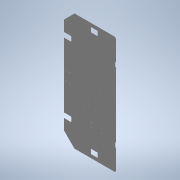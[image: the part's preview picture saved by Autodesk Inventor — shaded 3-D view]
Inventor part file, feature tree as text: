
AUTODESK INVENTOR PART (.ipt)
format: ipt  version: 2022.1 (Build 261234000, 234)  size: 481,792 bytes
history: native  units: mm
features: reference x12, other x11, sketch x3, sheet_metal_op x1, chamfer x1, extrude x1
ambient origin geometry x8: Origin, YZ Plane, XZ Plane, XY Plane, X Axis, Y Axis, Z Axis, Center Point
bodies: Solid1 (feature_tree)
feature tree (29):
  sheet_metal_op  "Face1"
  chamfer  "Corner Round1"
  extrude  "Extrusión1"  Depth=1.0mm
  sketch  "Sketch1"  dims[d1=1.0mm d2=1.0mm]
  reference  "Reference1"
  reference  "Reference2"
  reference  "Reference3"
  reference  "Reference4"
  reference  "Reference5"
  reference  "Reference6"
  other  "Plate1"
  reference  "Reference7"
  reference  "Reference8"
  reference  "Reference9"
  reference  "Reference10"
  reference  "Reference11"
  reference  "Reference12"
  sketch  "Boceto3"  dims[d3=1.0mm]
  sketch  "Boceto4"  dims[d4=1.0mm d5=1.0mm d6=1.0mm d7=1.0mm d10=1.0mm d15=1.0mm d16=0.5mm d17=4.0mm d18=1.0mm d19=1.0mm d20=1.0mm d21=1.0mm d22=1.0mm d24=1.0mm d38=250.0mm d39=67.0mm d40=108.0mm d41=2.9mm d42=2.9mm d43=2.9mm d44=2.9mm d45=250.0mm d46=44.0mm d47=66.0mm d48=1.8mm d49=1.8mm d50=1.8mm d51=1.8mm d52=44.0mm d53=0.0mm d54=66.0mm d55=44.0mm d57=19.0mm d58=44.0mm d59=66.0mm d60=1.8mm d61=1.8mm d62=1.8mm d63=1.8mm d64=1.8mm d65=1.8mm d66=1.8mm d67=1.8mm d68=58.0mm d69=80.0mm d71=4.5mm d72=4.5mm d73=80.0mm d74=95.0mm d75=20.0mm d76=67.0mm d77=108.0mm d78=2.9mm d79=2.9mm d80=2.9mm d81=2.9mm d84=36.9815mm d86=10.0mm d87=92.3mm d88=38.0mm d89=5.0mm d90=3.4mm d91=3.4mm d92=3.4mm d93=3.4mm d101=2.4mm d102=2.4mm d103=30.8356mm d105=20.75mm d106=3.4mm d107=3.4mm d108=3.4mm d109=3.4mm d110=86.999998mm d111=86.999998mm d112=100.269496mm d113=120.0mm d114=80.0mm d115=35.0mm d122=18.159314mm d123=10.372356mm d124=4.5mm d125=4.5mm d126=4.5mm d127=4.5mm d130=80.0mm d131=35.0mm d133=10.372356mm d134=4.5mm d135=4.5mm d136=4.5mm d137=4.5mm d139=12.55mm d140=45.0mm d141=4.5mm d142=4.5mm d145=40.0mm d146=60.0mm d147=30.0mm d148=157.0mm d149=3.4mm d150=110.0mm d151=95.16mm d152=25.0mm d153=2.9mm d154=35.0mm d155=33.02mm d156=63.5mm d157=80.0mm d158=0.5mm d159=0.0mm]
  other  "Cortar1"
  other  "<userpath>\Documents\2021-2\prueba final\ProyectoRobotPallet\RobotPallet.iam"
  other  "RobotPallet.iam"
  other  "EstructuraInferior:1"
  other  "Frame_Base:1"
  other  "ISO 10799-2 40x40x2 - 2899.41:1"
  other  "ISO 10799-2 40x40x2 - 444:1"
  other  "ISO 10799-2 40x40x2 - 211.1:2"
  other  "ISO 10799-2 40x40x2 - 211.1:1"
  other  "ISO 10799-2 40x40x2 - 464:2"
